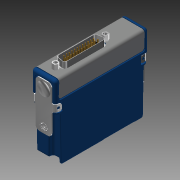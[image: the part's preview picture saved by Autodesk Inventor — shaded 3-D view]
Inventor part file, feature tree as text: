
AUTODESK INVENTOR PART (.ipt)
format: ipt  version: 2014 (Build 180170000, 170)  size: 8,076,800 bytes
history: native  units: mm
features: other x3, extrude x3, sketch x2, imported_body x1, fillet x1
ambient origin geometry x8: Origin, YZ Plane, XZ Plane, XY Plane, X Axis, Y Axis, Z Axis, Center Point
bodies: Solid1 (feature_tree)
feature tree (10):
  imported_body  "Base1"
  other  "RIGHT"
  other  "TOP"
  other  "FRONT"
  sketch  "Sketch3"  dims[d22=5.08mm d23=0.0mm]
  extrude  "Extrusion2"  Depth=10.0mm TaperAngle=0.0deg
  extrude  "Extrusion3"  [1 undecoded]
  sketch  "Sketch2"  dims[d0=25.4mm d1=2.54mm d3=10.0mm d5=130.0mm d6=25.4mm d7=2.54mm d9=10.0mm d11=120.0mm d12=1.397mm d13=1.397mm d14=1.27mm d15=1.008245mm d17=0.0mm d18=25.4mm d19=0.381mm d20=1.27mm d21=0.0mm]
  fillet  "Fillet1"  [1 undecoded]
  extrude  "Extrusion1"  [1 undecoded]
note: 3 required parameter values undecoded (feature->parameter linkage not recoverable at this tier; creation-order binding heuristic only, values carry confidence <= 0.55)
